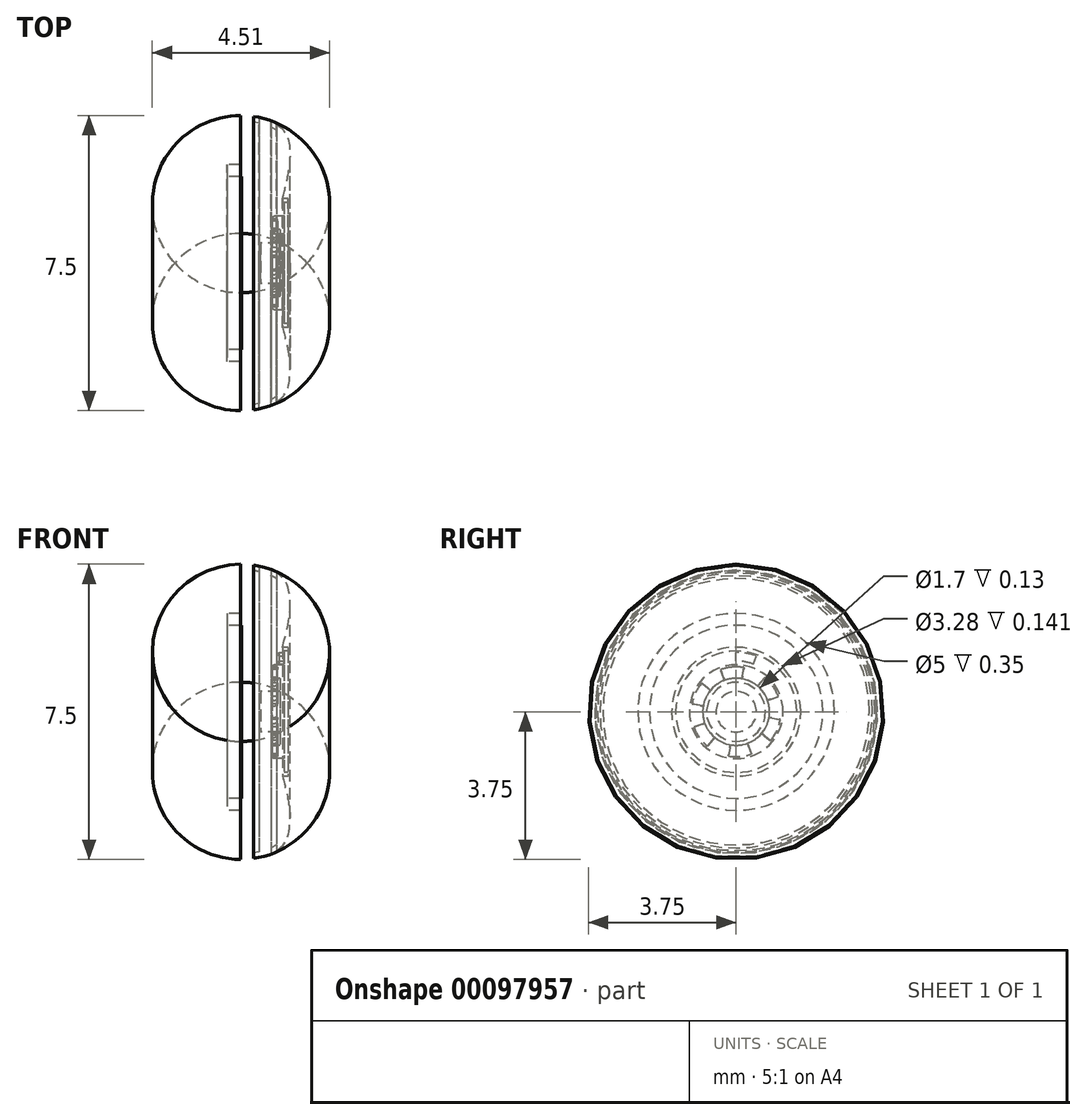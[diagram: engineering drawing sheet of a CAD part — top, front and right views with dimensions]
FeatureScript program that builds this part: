
annotation { "Feature Type Name" : "Feature", "Feature Type Description" : "" }
export const myFeature = defineFeature(function(context is Context, id is Id, definition is map)
    precondition{}
    {
        {
            var Q0;
            Q0=qCreatedBy(makeId("Front.planeOp"),FACE);
            var sketch = newSketch(context, id + "F0", { "sketchPlane" : qUnion([Q0])});
            skLineSegment(sketch, "E0.top", {"start": v(0.87, 0.85) * mm, "end": v(1, 0.85) * mm});
            skLineSegment(sketch, "E0.right", {"start": v(1, 0.51) * mm, "end": v(1, 0.85) * mm});
            skLineSegment(sketch, "E1", {"start": v(0.8, 0.93) * mm, "end": v(0.8, 1.1) * mm});
            skLineSegment(sketch, "E2", {"start": v(0.87, 1.19) * mm, "end": v(1.1, 1.19) * mm});
            skLineSegment(sketch, "E3", {"start": v(1.12, 1.64) * mm, "end": v(1.06, 1.64) * mm});
            skPoint(sketch, "E4.orphan", {"position": v(0, 1.19) * mm});
            skPoint(sketch, "E5.visualSharp", {"position": v(1.1, 1.19) * mm});
            skPoint(sketch, "E6.visualSharp", {"position": v(0.8, 1.19) * mm});
            skArc(sketch, "E6.filletArc", {"start": v(0.87, 1.19) * mm, "mid": v(0.81, 1.17) * mm, "end": v(0.8, 1.1) * mm});
            skArc(sketch, "E7.filletArc", {"start": v(0.8, 0.93) * mm, "mid": v(0.81, 0.87) * mm, "end": v(0.87, 0.85) * mm});
            skPoint(sketch, "E8.visualSharp", {"position": v(1.2, 1.64) * mm});
            skLineSegment(sketch, "E9", {"start": v(-0.76, 3.75) * mm, "end": v(0, 3.75) * mm, "construction": true});
            skLineSegment(sketch, "E10", {"start": v(1.25, 3.8) * mm, "end": v(1.25, 0.98) * mm, "construction": true});
            skLineSegment(sketch, "E11", {"start": v(0, 3.75) * mm, "end": v(1.72, 3.75) * mm, "construction": true});
            skLineSegment(sketch, "E12", {"start": v(1.25, 1.19) * mm, "end": v(1.27, 1.19) * mm});
            skLineSegment(sketch, "E13", {"start": v(1.1, 1.19) * mm, "end": v(1.1, 1.54) * mm});
            skPoint(sketch, "E14.orphan", {"position": v(0, 0.73) * mm});
            skLineSegment(sketch, "E15", {"start": v(0, 0.73) * mm, "end": v(0, 2.15) * mm, "construction": true});
            skLineSegment(sketch, "E16", {"start": v(0.5, 0.52) * mm, "end": v(1, 0.52) * mm});
            skLineSegment(sketch, "E17", {"start": v(0.57, 0) * mm, "end": v(0.57, -0.77) * mm, "construction": true});
            skLineSegment(sketch, "E18", {"start": v(1.1, 4.64) * mm, "end": v(1.1, 3.06) * mm, "construction": true});
            skLineSegment(sketch, "E19", {"start": v(0.97, 3.34) * mm, "end": v(1.1, 3.34) * mm, "construction": true});
            skFitSpline(sketch, "E20", {"points": [v(1.06, 1.64) * mm, v(1.25, 2.8) * mm, v(1.1, 3.34) * mm, v(0, 3.75) * mm], "startDerivative": vector(1.54, 5.67) * mm, "endDerivative": vector(-4.24, 0) * mm});
            skPoint(sketch, "E21", {"position": v(1.25, 2.38) * mm});
            skLineSegment(sketch, "E22", {"start": v(0.32, 3.93) * mm, "end": v(0.32, 3.59) * mm, "construction": true});
            skLineSegment(sketch, "E23", {"start": v(0.46, 3.93) * mm, "end": v(0.46, 3.56) * mm, "construction": true});
            skLineSegment(sketch, "E24", {"start": v(0.77, 3.93) * mm, "end": v(0.77, 3.46) * mm, "construction": true});
            skLineSegment(sketch, "E25", {"start": v(0.91, 3.95) * mm, "end": v(0.91, 3.38) * mm, "construction": true});
            skLineSegment(sketch, "E26", {"start": v(0.32, 3.59) * mm, "end": v(0.46, 3.56) * mm});
            skLineSegment(sketch, "E27", {"start": v(0.77, 3.46) * mm, "end": v(0.91, 3.38) * mm});
            skLineSegment(sketch, "E28", {"start": v(0.32, 3.73) * mm, "end": v(0.32, 3.59) * mm});
            skLineSegment(sketch, "E29", {"start": v(0.46, 3.56) * mm, "end": v(0.46, 3.7) * mm});
            skLineSegment(sketch, "E30", {"start": v(0.77, 3.46) * mm, "end": v(0.77, 3.6) * mm});
            skLineSegment(sketch, "E31", {"start": v(0.91, 3.38) * mm, "end": v(0.91, 3.52) * mm});
            skLineSegment(sketch, "E32", {"start": v(0, 0.52) * mm, "end": v(0, 2.15) * mm});
            skLineSegment(sketch, "E33", {"start": v(0.02, 0) * mm, "end": v(2.08, 0) * mm, "construction": true});
            skLineSegment(sketch, "E34", {"start": v(0, 0.51) * mm, "end": v(0, 2.15) * mm, "construction": true});
            skLineSegment(sketch, "E35", {"start": v(0, 0.52) * mm, "end": v(0, 0) * mm});
            skLineSegment(sketch, "E36", {"start": v(0, 0) * mm, "end": v(0.5, 0) * mm});
            skLineSegment(sketch, "E37", {"start": v(0.5, 0) * mm, "end": v(0.5, 0.52) * mm});
            skLineSegment(sketch, "E38", {"start": v(1.2, 1.54) * mm, "end": v(1.1, 1.54) * mm});
            skLineSegment(sketch, "E39", {"start": v(1.2, 1.64) * mm, "end": v(1.12, 1.64) * mm});
            skLineSegment(sketch, "E40", {"start": v(1.2, 1.64) * mm, "end": v(1.2, 1.54) * mm});
            skLineSegment(sketch, "E41", {"start": v(0, 2.75) * mm, "end": v(0.2, 2.75) * mm, "construction": true});
            skLineSegment(sketch, "E42", {"start": v(0.2, 2.75) * mm, "end": v(0.2, 2.55) * mm, "construction": true});
            skLineSegment(sketch, "E43", {"start": v(0.2, 2.55) * mm, "end": v(0.5, 2.55) * mm, "construction": true});
            skLineSegment(sketch, "E44", {"start": v(0.5, 2.55) * mm, "end": v(0.5, 2.15) * mm, "construction": true});
            skLineSegment(sketch, "E45", {"start": v(0.5, 2.15) * mm, "end": v(0.02, 2.15) * mm, "construction": true});
            skLineSegment(sketch, "E46.trimOffspring", {"start": v(0, 2.75) * mm, "end": v(0, 5.56) * mm, "construction": true});
            skLineSegment(sketch, "E47.trimOffspring", {"start": v(0, 2.75) * mm, "end": v(0, 5.2) * mm, "construction": true});
            skLineSegment(sketch, "E48.trimOffspring", {"start": v(0, 2.75) * mm, "end": v(0, 3.75) * mm});
            skLineSegment(sketch, "E49", {"start": v(0.02, 0) * mm, "end": v(0.02, 2.15) * mm});
            skLineSegment(sketch, "E50", {"start": v(0, 2.75) * mm, "end": v(0, 2.5) * mm});
            skLineSegment(sketch, "E51", {"start": v(0, 2.5) * mm, "end": v(-0.35, 2.5) * mm});
            skLineSegment(sketch, "E52", {"start": v(-0.35, 2.5) * mm, "end": v(-0.35, 2.2) * mm});
            skLineSegment(sketch, "E53", {"start": v(-0.35, 2.2) * mm, "end": v(0.02, 2.2) * mm});
            skLineSegment(sketch, "E54", {"start": v(0.02, 2.2) * mm, "end": v(0.02, 2.15) * mm});
            skSolve(sketch);
        }
        {
            var Q0;
            Q0=makeQuery(id+"F0.imprint","IMPRINT",FACE,{"disambiguationData":[TD([[makeQuery(id+"F0.imprint","IMPRINT",EDGE,{"derivedFrom":sQuery(id+"F0.wireOp",EDGE,"E0.top")}),-1.0]])]});
            var Q1;
            Q1=sQuery(id+"F0.wireOp",EDGE,"8bb111fc-4642-4fca-a44e-8b574824e9490.MirrorCS");
            var Q2;
            Q2=sQuery(id+"F0.wireOp",EDGE,"5d76dffb-9663-4801-85ba-127905f750e50.MirrorCS");
            var Q3;
            Q3=sQuery(id+"F0.wireOp",EDGE,"d13460d5-a523-4224-9297-77c6a2cba0c50.MirrorCS");
            var Q4;
            Q4=sQuery(id+"F0.wireOp",EDGE,"c0737af9-8dda-4185-ab45-cae04200aa6d0.MirrorCS");
            var Q5;
            Q5=sQuery(id+"F0.wireOp",EDGE,"E33");
            revolve(context, id + "F1", {"entities" : qUnion([Q0]), "surfaceEntities" : qUnion([Q1, Q2, Q3, Q4]), "axis" : qUnion([Q5]), "revolveType" : RevolveType.FULL});
        }
        {
            var Q0;
            Q0=qCreatedBy(makeId("Front.planeOp"),FACE);
            var sketch = newSketch(context, id + "F2", { "sketchPlane" : qUnion([Q0])});
            skLineSegment(sketch, "E55.bottom", {"start": v(0.97, 1.51) * mm, "end": v(1.17, 1.51) * mm});
            skLineSegment(sketch, "E55.top", {"start": v(0.97, 1.29) * mm, "end": v(1.17, 1.29) * mm});
            skLineSegment(sketch, "E55.left", {"start": v(0.97, 1.51) * mm, "end": v(0.97, 1.29) * mm});
            skLineSegment(sketch, "E55.right", {"start": v(1.17, 1.51) * mm, "end": v(1.17, 1.29) * mm});
            skLineSegment(sketch, "E56", {"start": v(0, 0) * mm, "end": v(2.72, 0) * mm, "construction": true});
            skSolve(sketch);
        }
        {
            var Q0;
            Q0=qSketchRegion(id+"F2",true);
            var Q1;
            Q1=sQuery(id+"F2.wireOp",EDGE,"E56");
            revolve(context, id + "F3", {"operationType" : NewBodyOperationType.REMOVE, "entities" : qUnion([Q0]), "axis" : qUnion([Q1]), "revolveType" : RevolveType.ONE_DIRECTION, "oppositeDirection" : true, "angle" : 20 * degree});
        }
        {
            var Q0;
            Q0=makeQuery(id+"F1.opRevolve","SWEPT_FACE",FACE,{"disambiguationData":[OSD([sQuery(id+"F0.wireOp",EDGE,"E1")])]});
            var sketch = newSketch(context, id + "F4", { "sketchPlane" : qUnion([Q0])});
            skLineSegment(sketch, "E57", {"start": v(-0.27, 0.74) * mm, "end": v(-0.39, 1.07) * mm});
            skArc(sketch, "E58", {"start": v(-0.39, 1.07) * mm, "mid": v(-0.1, 1.13) * mm, "end": v(0.2, 1.12) * mm});
            skLineSegment(sketch, "E59", {"start": v(0.14, 0.78) * mm, "end": v(0.2, 1.12) * mm});
            skArc(sketch, "E60", {"start": v(-0.27, 0.74) * mm, "mid": v(-0.07, 0.79) * mm, "end": v(0.14, 0.78) * mm});
            skLineSegment(sketch, "E61.1.0", {"start": v(-0.78, 0.14) * mm, "end": v(-1.12, 0.2) * mm});
            skArc(sketch, "E61.1.1", {"start": v(-1.12, 0.2) * mm, "mid": v(-1.03, 0.48) * mm, "end": v(-0.87, 0.73) * mm});
            skLineSegment(sketch, "E61.1.2", {"start": v(-0.6, 0.5) * mm, "end": v(-0.87, 0.73) * mm});
            skArc(sketch, "E61.1.3", {"start": v(-0.78, 0.14) * mm, "mid": v(-0.71, 0.33) * mm, "end": v(-0.6, 0.5) * mm});
            skLineSegment(sketch, "E61.2.0", {"start": v(-0.5, -0.6) * mm, "end": v(-0.73, -0.87) * mm});
            skArc(sketch, "E61.2.1", {"start": v(-0.73, -0.87) * mm, "mid": v(-0.93, -0.65) * mm, "end": v(-1.07, -0.39) * mm});
            skLineSegment(sketch, "E61.2.2", {"start": v(-0.74, -0.27) * mm, "end": v(-1.07, -0.39) * mm});
            skArc(sketch, "E61.2.3", {"start": v(-0.5, -0.6) * mm, "mid": v(-0.65, -0.45) * mm, "end": v(-0.74, -0.27) * mm});
            skLineSegment(sketch, "E62.1.3.0", {"start": v(0.27, -0.74) * mm, "end": v(0.39, -1.07) * mm});
            skArc(sketch, "E62.3.3.0", {"start": v(0.39, -1.07) * mm, "mid": v(0.1, -1.13) * mm, "end": v(-0.2, -1.12) * mm});
            skLineSegment(sketch, "E62.7.3.0", {"start": v(-0.14, -0.78) * mm, "end": v(-0.2, -1.12) * mm});
            skArc(sketch, "E62.10.3.0", {"start": v(0.27, -0.74) * mm, "mid": v(0.07, -0.79) * mm, "end": v(-0.14, -0.78) * mm});
            skLineSegment(sketch, "E62.1.4.0", {"start": v(0.78, -0.14) * mm, "end": v(1.12, -0.2) * mm});
            skArc(sketch, "E62.3.4.0", {"start": v(1.12, -0.2) * mm, "mid": v(1.03, -0.48) * mm, "end": v(0.87, -0.73) * mm});
            skLineSegment(sketch, "E62.7.4.0", {"start": v(0.6, -0.5) * mm, "end": v(0.87, -0.73) * mm});
            skArc(sketch, "E62.10.4.0", {"start": v(0.78, -0.14) * mm, "mid": v(0.71, -0.33) * mm, "end": v(0.6, -0.5) * mm});
            skLineSegment(sketch, "E62.1.5.0", {"start": v(0.5, 0.6) * mm, "end": v(0.73, 0.87) * mm});
            skArc(sketch, "E62.3.5.0", {"start": v(0.73, 0.87) * mm, "mid": v(0.93, 0.65) * mm, "end": v(1.07, 0.39) * mm});
            skLineSegment(sketch, "E62.7.5.0", {"start": v(0.74, 0.27) * mm, "end": v(1.07, 0.39) * mm});
            skArc(sketch, "E62.10.5.0", {"start": v(0.5, 0.6) * mm, "mid": v(0.65, 0.45) * mm, "end": v(0.74, 0.27) * mm});
            skSolve(sketch);
        }
        {
            var Q0;
            Q0=qSketchRegion(id+"F4",true);
            extrude(context, id + "F5", {"entities" : qUnion([Q0]), "operationType" : NewBodyOperationType.ADD, "depth" : .15 * mm});
        }
    });
